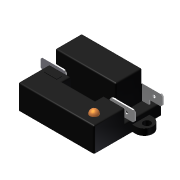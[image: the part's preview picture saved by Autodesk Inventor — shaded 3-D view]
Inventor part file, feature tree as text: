
AUTODESK INVENTOR PART (.ipt)
format: ipt  version: 2013 (Build 170138000, 138)  size: 338,944 bytes
history: native  units: mm (DEFAULTED — no unit token found)
features: other x1, fillet x1, imported_body x1
ambient origin geometry x8: Origin, YZ Plane, XZ Plane, XY Plane, X Axis, Y Axis, Z Axis, Center Point
bodies: Solid1 (feature_tree)
feature tree (3):
  other  "Spike Relay.ipt"
  fillet  "Fillet1"  Radius=0.762mm
  imported_body  "DerivedBody::Spike Relay.ipt"
